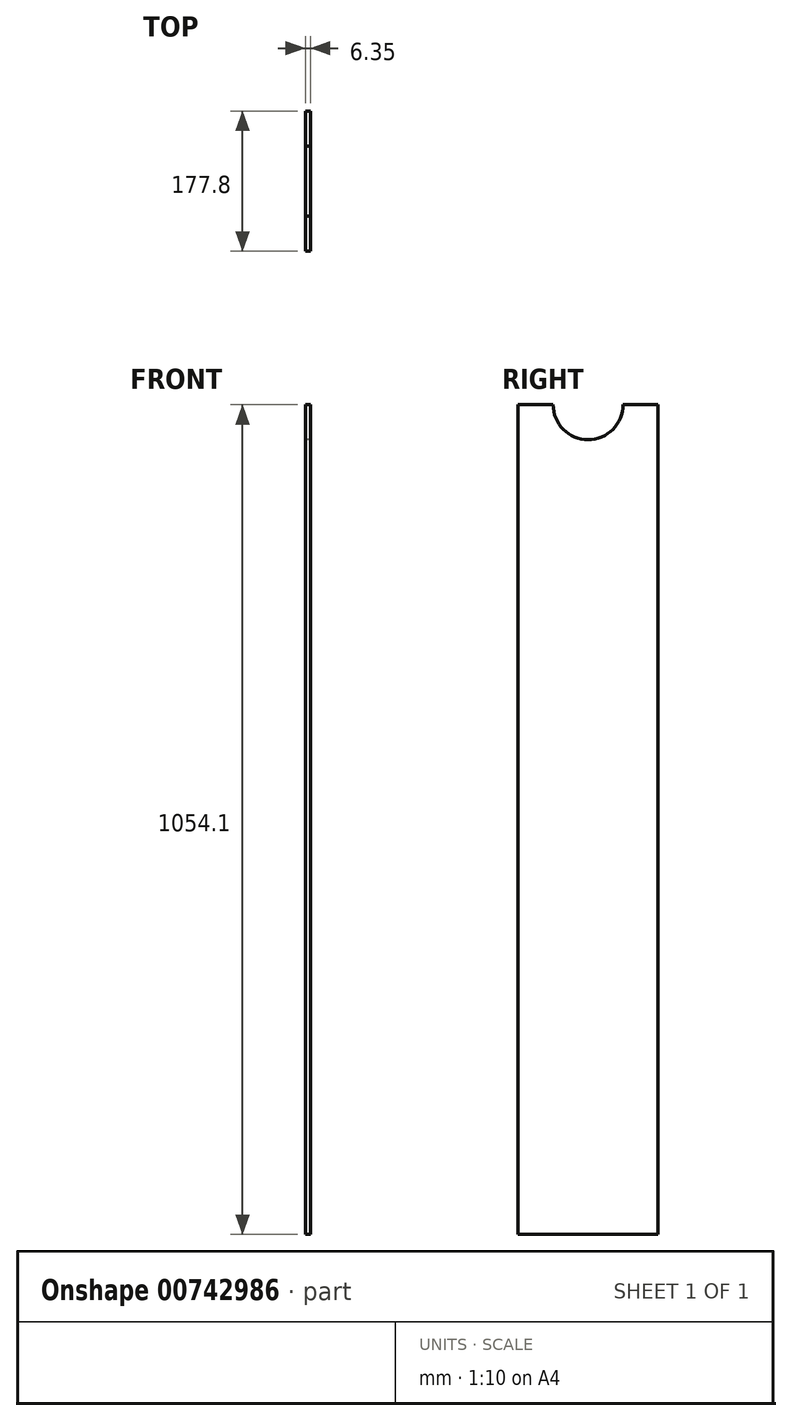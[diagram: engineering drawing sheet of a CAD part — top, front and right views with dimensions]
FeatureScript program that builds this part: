
annotation { "Feature Type Name" : "Feature", "Feature Type Description" : "" }
export const myFeature = defineFeature(function(context is Context, id is Id, definition is map)
    precondition{}
    {
        {
            var Q0;
            Q0=qCreatedBy(makeId("Right.planeOp"),FACE);
            var sketch = newSketch(context, id + "F0", { "sketchPlane" : qUnion([Q0])});
            skLineSegment(sketch, "E0.bottom", {"start": v(88.9, 527.05) * mm, "end": v(-88.9, 527.05) * mm});
            skLineSegment(sketch, "E0.top", {"start": v(88.9, -527.05) * mm, "end": v(-88.9, -527.05) * mm});
            skLineSegment(sketch, "E0.left", {"start": v(88.9, 527.05) * mm, "end": v(88.9, -527.05) * mm});
            skLineSegment(sketch, "E0.right", {"start": v(-88.9, 527.05) * mm, "end": v(-88.9, -527.05) * mm});
            skPoint(sketch, "E0.middle", {"position": v(0, 0) * mm});
            skCircle(sketch, "E1", {"center": v(0, 527.05) * mm, "radius": 44.45 * mm});
            skSolve(sketch);
        }
        {
            var Q0;
            Q0=makeQuery(id+"F0.imprint","IMPRINT",FACE,{"disambiguationData":[TD([[makeQuery(id+"F0.imprint","IMPRINT",EDGE,{"derivedFrom":sQuery(id+"F0.wireOp",EDGE,"E0.bottom")}),1.0]])]});
            extrude(context, id + "F1", {"entities" : qUnion([Q0]), "depth" : 6.35 * mm, "offsetDistance" : 25.4 * mm});
        }
    });
